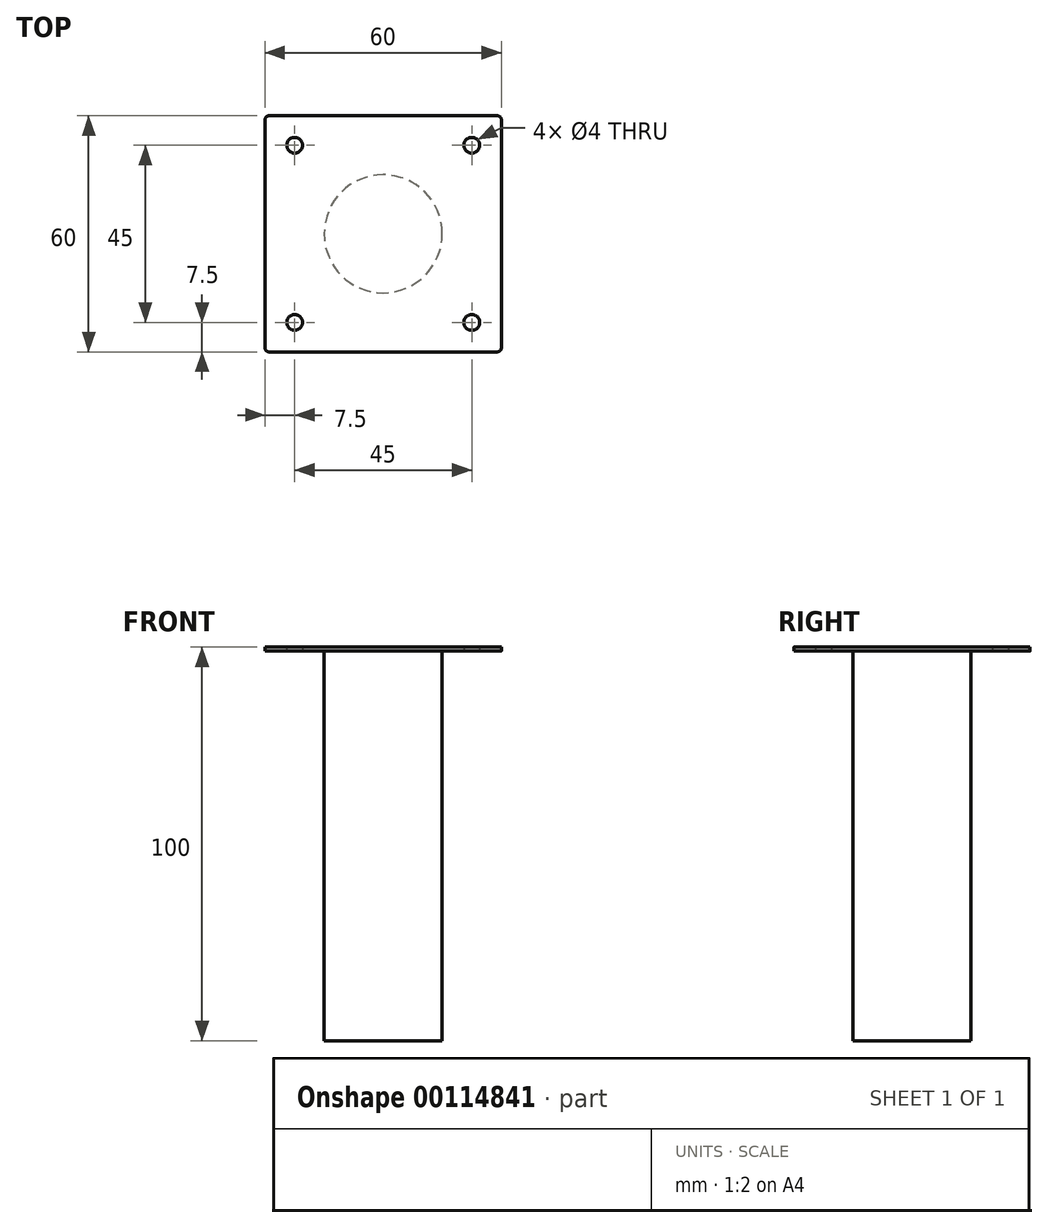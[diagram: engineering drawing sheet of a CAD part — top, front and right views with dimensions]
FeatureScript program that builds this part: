
annotation { "Feature Type Name" : "Feature", "Feature Type Description" : "" }
export const myFeature = defineFeature(function(context is Context, id is Id, definition is map)
    precondition{}
    {
        {
            var Q0;
            Q0=qCreatedBy(makeId("Top.planeOp"),FACE);
            var sketch = newSketch(context, id + "F0", { "sketchPlane" : qUnion([Q0])});
            skLineSegment(sketch, "E0.bottom", {"start": v(-29, -30) * mm, "end": v(29, -30) * mm});
            skLineSegment(sketch, "E0.top", {"start": v(-29, 30) * mm, "end": v(29, 30) * mm});
            skLineSegment(sketch, "E0.left", {"start": v(-30, -29) * mm, "end": v(-30, 29) * mm});
            skLineSegment(sketch, "E0.right", {"start": v(30, -29) * mm, "end": v(30, 29) * mm});
            skPoint(sketch, "E0.middle", {"position": v(0, 0) * mm});
            skLineSegment(sketch, "E1", {"start": v(-30, -22.5) * mm, "end": v(30, -22.5) * mm, "construction": true});
            skLineSegment(sketch, "E2", {"start": v(-22.5, -30) * mm, "end": v(-22.5, 30) * mm, "construction": true});
            skLineSegment(sketch, "E3", {"start": v(-30, 22.5) * mm, "end": v(30, 22.5) * mm, "construction": true});
            skLineSegment(sketch, "E4", {"start": v(22.5, -30) * mm, "end": v(22.5, 30) * mm, "construction": true});
            skPoint(sketch, "E5.visualSharp", {"position": v(-30, -30) * mm});
            skArc(sketch, "E5.filletArc", {"start": v(-30, -29) * mm, "mid": v(-29.7, -29.7) * mm, "end": v(-29, -30) * mm});
            skPoint(sketch, "E6.visualSharp", {"position": v(30, -30) * mm});
            skArc(sketch, "E6.filletArc", {"start": v(29, -30) * mm, "mid": v(29.7, -29.7) * mm, "end": v(30, -29) * mm});
            skPoint(sketch, "E7.visualSharp", {"position": v(30, 30) * mm});
            skArc(sketch, "E7.filletArc", {"start": v(30, 29) * mm, "mid": v(29.7, 29.7) * mm, "end": v(29, 30) * mm});
            skPoint(sketch, "E8.visualSharp", {"position": v(-30, 30) * mm});
            skArc(sketch, "E8.filletArc", {"start": v(-29, 30) * mm, "mid": v(-29.7, 29.7) * mm, "end": v(-30, 29) * mm});
            skCircle(sketch, "E9", {"center": v(-22.5, -22.5) * mm, "radius": 2 * mm});
            skCircle(sketch, "E10", {"center": v(22.5, -22.5) * mm, "radius": 2 * mm});
            skCircle(sketch, "E11", {"center": v(-22.5, 22.5) * mm, "radius": 2 * mm});
            skCircle(sketch, "E12", {"center": v(22.5, 22.5) * mm, "radius": 2 * mm});
            skSolve(sketch);
        }
        {
            var Q0;
            Q0=makeQuery(id+"F0.imprint","IMPRINT",FACE,{"disambiguationData":[TD([[makeQuery(id+"F0.imprint","IMPRINT",EDGE,{"derivedFrom":sQuery(id+"F0.wireOp",EDGE,"E0.bottom")}),1.0]])]});
            extrude(context, id + "F1", {"entities" : qUnion([Q0]), "depth" : 1 * mm});
        }
        {
            var Q0;
            Q0=makeQuery(id+"F1.opExtrude","CAP_FACE",FACE,{"disambiguationData":[OSD([sQuery(id+"F0.wireOp",EDGE,"E0.bottom"),sQuery(id+"F0.wireOp",EDGE,"E0.top"),sQuery(id+"F0.wireOp",EDGE,"E0.left"),sQuery(id+"F0.wireOp",EDGE,"E0.right"),sQuery(id+"F0.wireOp",EDGE,"E5.filletArc"),sQuery(id+"F0.wireOp",EDGE,"E6.filletArc"),sQuery(id+"F0.wireOp",EDGE,"E7.filletArc"),sQuery(id+"F0.wireOp",EDGE,"E8.filletArc"),sQuery(id+"F0.wireOp",EDGE,"E9"),sQuery(id+"F0.wireOp",EDGE,"E10"),sQuery(id+"F0.wireOp",EDGE,"E11"),sQuery(id+"F0.wireOp",EDGE,"E12")])],"isStart":true});
            var sketch = newSketch(context, id + "F2", { "sketchPlane" : qUnion([Q0])});
            skCircle(sketch, "E13", {"center": v(0, 0) * mm, "radius": 15 * mm});
            skSolve(sketch);
        }
        {
            var Q0;
            Q0 = qSketchRegion(id + "F2", true);
            extrude(context, id + "F3", {"entities" : qUnion([Q0]), "operationType" : NewBodyOperationType.ADD, "depth" : 99 * mm});
        }
    });
